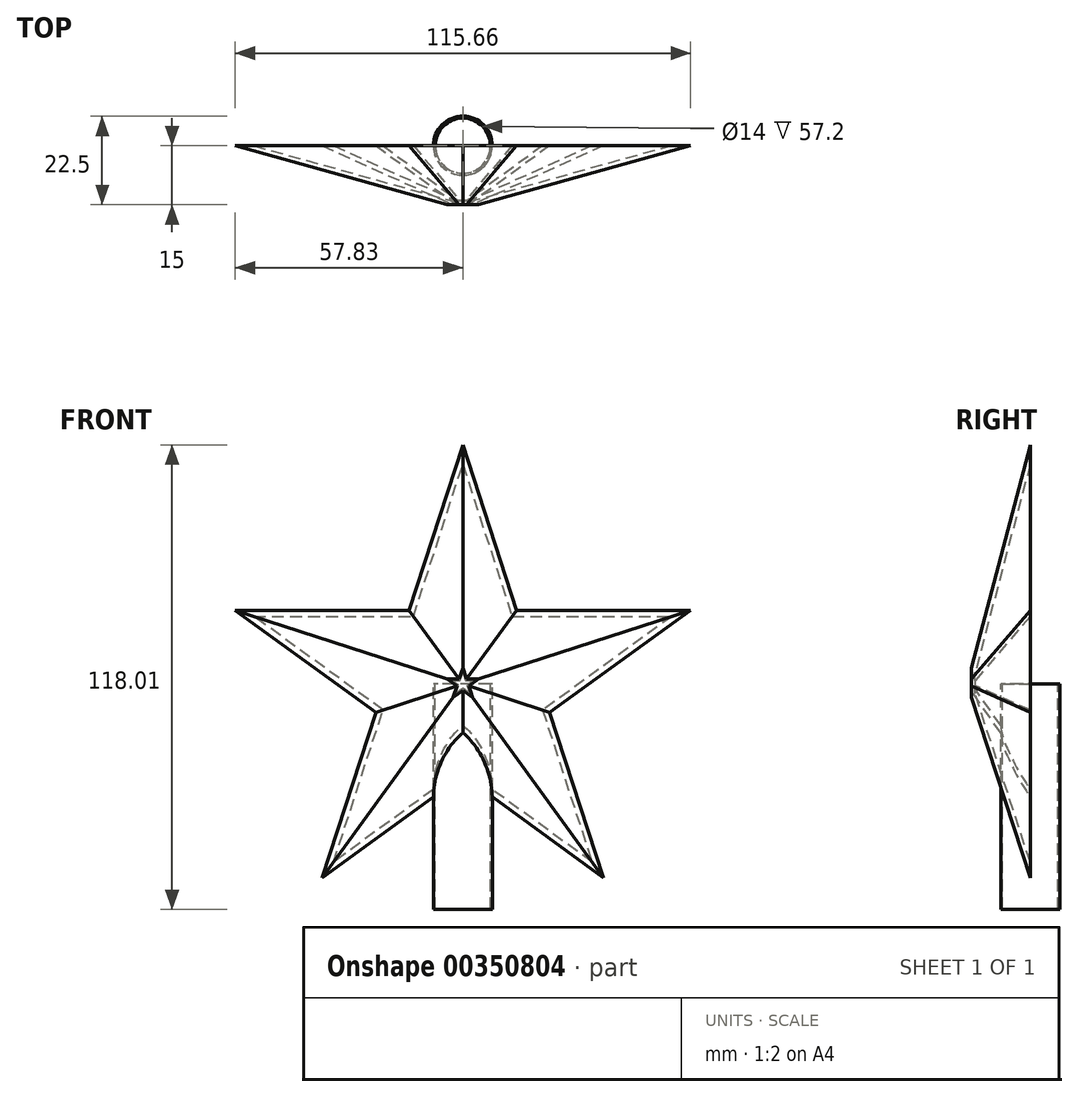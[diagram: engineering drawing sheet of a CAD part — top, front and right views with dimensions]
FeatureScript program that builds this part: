
annotation { "Feature Type Name" : "Feature", "Feature Type Description" : "" }
export const myFeature = defineFeature(function(context is Context, id is Id, definition is map)
    precondition{}
    {
        {
            var Q0;
            Q0=qCreatedBy(makeId("Front.planeOp"),FACE);
            var sketch = newSketch(context, id + "F0", { "sketchPlane" : qUnion([Q0])});
            skCircle(sketch, "E0.cCircle", {"center": v(0, 0) * mm, "radius": 18.8 * mm, "construction": true});
            skLineSegment(sketch, "E0.0", {"start": v(-13.65, 18.8) * mm, "end": v(13.65, 18.8) * mm, "construction": true});
            skLineSegment(sketch, "E0.1", {"start": v(13.65, 18.8) * mm, "end": v(22.09, -7.18) * mm, "construction": true});
            skLineSegment(sketch, "E0.2", {"start": v(22.09, -7.18) * mm, "end": v(0, -23.23) * mm, "construction": true});
            skLineSegment(sketch, "E0.3", {"start": v(0, -23.23) * mm, "end": v(-22.09, -7.18) * mm, "construction": true});
            skLineSegment(sketch, "E0.4", {"start": v(-22.09, -7.18) * mm, "end": v(-13.65, 18.8) * mm, "construction": true});
            skPoint(sketch, "E0.0.midPoint", {"position": v(0, 18.8) * mm});
            skLineSegment(sketch, "E1", {"start": v(-13.65, 18.8) * mm, "end": v(0, 60.8) * mm});
            skLineSegment(sketch, "E2", {"start": v(0, 60.8) * mm, "end": v(13.65, 18.8) * mm});
            skLineSegment(sketch, "E3", {"start": v(13.65, 18.8) * mm, "end": v(57.83, 18.8) * mm});
            skLineSegment(sketch, "E4", {"start": v(57.83, 18.8) * mm, "end": v(22.09, -7.18) * mm});
            skLineSegment(sketch, "E5", {"start": v(22.09, -7.18) * mm, "end": v(35.74, -49.2) * mm});
            skLineSegment(sketch, "E6", {"start": v(35.74, -49.2) * mm, "end": v(0, -23.23) * mm});
            skLineSegment(sketch, "E7", {"start": v(0, -23.23) * mm, "end": v(-35.74, -49.2) * mm});
            skLineSegment(sketch, "E8", {"start": v(-35.74, -49.2) * mm, "end": v(-22.09, -7.18) * mm});
            skLineSegment(sketch, "E9", {"start": v(-22.09, -7.18) * mm, "end": v(-57.83, 18.8) * mm});
            skLineSegment(sketch, "E10", {"start": v(-57.83, 18.8) * mm, "end": v(-13.65, 18.8) * mm});
            skSolve(sketch);
        }
        {
            var Q0;
            Q0=qCreatedBy(makeId("Front.planeOp"),FACE);
            cPlane(context, id + "F1", {"entities" : qUnion([Q0]), "cplaneType" : CPlaneType.OFFSET, "offset" : 15 * mm, "width" : 150 * mm, "height" : 150 * mm});
        }
        {
            var Q0;
            Q0=qCreatedBy(id+"F1.planeOp",FACE);
            var sketch = newSketch(context, id + "F2", { "sketchPlane" : qUnion([Q0])});
            skCircle(sketch, "E11.0", {"center": v(0, 0) * mm, "radius": 18.8 * mm, "construction": true});
            skLineSegment(sketch, "E11.1", {"start": v(-13.65, 18.8) * mm, "end": v(13.65, 18.8) * mm, "construction": true});
            skLineSegment(sketch, "E11.2", {"start": v(13.65, 18.8) * mm, "end": v(22.09, -7.18) * mm, "construction": true});
            skLineSegment(sketch, "E11.3", {"start": v(22.09, -7.18) * mm, "end": v(0, -23.23) * mm, "construction": true});
            skLineSegment(sketch, "E11.4", {"start": v(0, -23.23) * mm, "end": v(-22.09, -7.18) * mm, "construction": true});
            skLineSegment(sketch, "E11.5", {"start": v(-22.09, -7.18) * mm, "end": v(-13.65, 18.8) * mm, "construction": true});
            skPoint(sketch, "E11.6", {"position": v(0, 18.8) * mm});
            skLineSegment(sketch, "E11.7", {"start": v(-13.65, 18.8) * mm, "end": v(0, 60.8) * mm, "construction": true});
            skLineSegment(sketch, "E11.8", {"start": v(0, 60.8) * mm, "end": v(13.65, 18.8) * mm, "construction": true});
            skLineSegment(sketch, "E11.9", {"start": v(13.65, 18.8) * mm, "end": v(57.83, 18.8) * mm, "construction": true});
            skLineSegment(sketch, "E11.10", {"start": v(57.83, 18.8) * mm, "end": v(22.09, -7.18) * mm, "construction": true});
            skLineSegment(sketch, "E11.11", {"start": v(22.09, -7.18) * mm, "end": v(35.74, -49.2) * mm, "construction": true});
            skLineSegment(sketch, "E11.12", {"start": v(35.74, -49.2) * mm, "end": v(0, -23.23) * mm, "construction": true});
            skLineSegment(sketch, "E11.13", {"start": v(0, -23.23) * mm, "end": v(-35.74, -49.2) * mm, "construction": true});
            skLineSegment(sketch, "E11.14", {"start": v(-35.74, -49.2) * mm, "end": v(-22.09, -7.18) * mm, "construction": true});
            skLineSegment(sketch, "E11.15", {"start": v(-22.09, -7.18) * mm, "end": v(-57.83, 18.8) * mm, "construction": true});
            skLineSegment(sketch, "E11.16", {"start": v(-57.83, 18.8) * mm, "end": v(-13.65, 18.8) * mm, "construction": true});
            skLineSegment(sketch, "E12.0", {"start": v(-0.94, 1.3) * mm, "end": v(0, 4.18) * mm});
            skLineSegment(sketch, "E12.1", {"start": v(-3.97, 1.3) * mm, "end": v(-0.94, 1.3) * mm});
            skLineSegment(sketch, "E12.2", {"start": v(0, 4.18) * mm, "end": v(0.94, 1.3) * mm});
            skLineSegment(sketch, "E12.3", {"start": v(-1.52, -0.5) * mm, "end": v(-3.97, 1.3) * mm});
            skLineSegment(sketch, "E12.4", {"start": v(-2.45, -3.38) * mm, "end": v(-1.52, -0.5) * mm});
            skLineSegment(sketch, "E12.5", {"start": v(0, -1.6) * mm, "end": v(-2.45, -3.38) * mm});
            skLineSegment(sketch, "E12.6", {"start": v(0.94, 1.3) * mm, "end": v(3.97, 1.3) * mm});
            skLineSegment(sketch, "E12.7", {"start": v(3.97, 1.3) * mm, "end": v(1.52, -0.5) * mm});
            skLineSegment(sketch, "E12.8", {"start": v(1.52, -0.5) * mm, "end": v(2.45, -3.38) * mm});
            skLineSegment(sketch, "E12.9", {"start": v(2.45, -3.38) * mm, "end": v(0, -1.6) * mm});
            skSolve(sketch);
        }
        {
            var Q0;
            Q0=makeQuery(id+"F0.imprint","IMPRINT",FACE,{"disambiguationData":[TD([[makeQuery(id+"F0.imprint","IMPRINT",EDGE,{"derivedFrom":sQuery(id+"F0.wireOp",EDGE,"E1")}),-1.0]])]});
            var Q1;
            Q1=makeQuery(id+"F2.imprint","IMPRINT",FACE,{"disambiguationData":[TD([[makeQuery(id+"F2.imprint","IMPRINT",EDGE,{"derivedFrom":sQuery(id+"F2.wireOp",EDGE,"E12.0")}),-1.0]])]});
            loft(context, id + "F3", {"sheetProfilesArray" : [{ "sheetProfileEntities" : qUnion([Q0]) }, { "sheetProfileEntities" : qUnion([Q1]) }]});
        }
        {
            var Q0;
            Q0=makeQuery(id+"F3.opLoft","CAP_FACE",FACE,{"disambiguationData":[OSD([makeQuery(id+"F0.imprint","IMPRINT",FACE,{"disambiguationData":[TD([[makeQuery(id+"F0.imprint","IMPRINT",EDGE,{"derivedFrom":sQuery(id+"F0.wireOp",EDGE,"E1")}),-1.0]])]})])],"isStart":true});
            shell(context, id + "F4", {"entities" : qUnion([Q0]), "thickness" : 1 * mm});
        }
        {
            var Q0;
            Q0=qCreatedBy(makeId("Top.planeOp"),FACE);
            var sketch = newSketch(context, id + "F5", { "sketchPlane" : qUnion([Q0])});
            skCircle(sketch, "E13", {"center": v(0, 0) * mm, "radius": 7.5 * mm});
            skSolve(sketch);
        }
        {
            var Q0;
            Q0 = qSketchRegion(id + "F5", true);
            extrude(context, id + "F6", {"entities" : qUnion([Q0]), "operationType" : NewBodyOperationType.REMOVE, "endBound" : BoundingType.THROUGH_ALL, "oppositeDirection" : true, "depth" : 25 * mm});
        }
        {
            var Q0;
            Q0=qCreatedBy(makeId("Top.planeOp"),FACE);
            var sketch = newSketch(context, id + "F7", { "sketchPlane" : qUnion([Q0])});
            skCircle(sketch, "E14", {"center": v(0, 0) * mm, "radius": 7.5 * mm});
            skCircle(sketch, "E15", {"center": v(0, 0) * mm, "radius": 7 * mm});
            skSolve(sketch);
        }
        {
            var Q0;
            Q0=makeQuery(id+"F7.imprint","IMPRINT",FACE,{"disambiguationData":[TD([[makeQuery(id+"F7.imprint","IMPRINT",EDGE,{"derivedFrom":sQuery(id+"F7.wireOp",EDGE,"E14")}),1.0]])]});
            extrude(context, id + "F8", {"entities" : qUnion([Q0]), "operationType" : NewBodyOperationType.ADD, "oppositeDirection" : true, "depth" : 50 * mm});
        }
        {
            var Q0;
            Q0=makeQuery(id+"F8.opExtrude","CAP_FACE",FACE,{"disambiguationData":[OSD([sQuery(id+"F7.wireOp",EDGE,"E14"),sQuery(id+"F7.wireOp",EDGE,"E15")])],"isStart":true});
            var sketch = newSketch(context, id + "F9", { "sketchPlane" : qUnion([Q0])});
            skCircle(sketch, "E16.0", {"center": v(0, 0) * mm, "radius": 7.5 * mm});
            skSolve(sketch);
        }
        {
            var Q0;
            Q0 = qSketchRegion(id + "F9", true);
            extrude(context, id + "F10", {"entities" : qUnion([Q0]), "operationType" : NewBodyOperationType.REMOVE, "oppositeDirection" : true, "depth" : 10 * mm});
        }
        {
            var Q0;
            Q0=qCreatedBy(makeId("Front.planeOp"),FACE);
            var sketch = newSketch(context, id + "F11", { "sketchPlane" : qUnion([Q0])});
            skCircle(sketch, "E17", {"center": v(0, 0) * mm, "radius": 67.09 * mm});
            skSolve(sketch);
        }
        {
            var Q0;
            Q0 = qSketchRegion(id + "F11", true);
            extrude(context, id + "F12", {"entities" : qUnion([Q0]), "operationType" : NewBodyOperationType.REMOVE, "oppositeDirection" : true, "depth" : 25 * mm});
        }
        {
            var Q0;
            Q0 = qSketchRegion(id + "F7", true);
            extrude(context, id + "F13", {"entities" : qUnion([Q0]), "operationType" : NewBodyOperationType.ADD, "oppositeDirection" : true, "depth" : 57.2 * mm});
        }
    });
